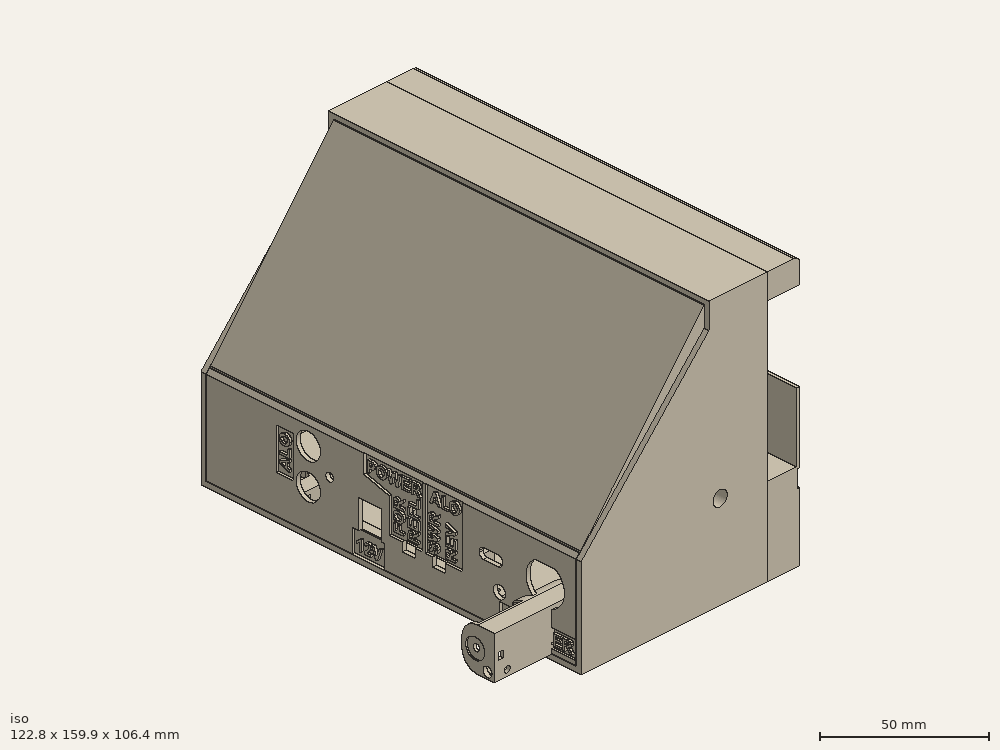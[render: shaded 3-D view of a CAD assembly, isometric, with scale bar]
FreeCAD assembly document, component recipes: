
FREECAD ASSEMBLY — COMPONENT RECIPES ("console")

This assembly document has 6 components, labeled P0..P5 below (a component is one placed body or linked part). 5 of them carry a construction recipe — the FreeCAD feature program that regenerates the part from scratch, quoted from this document or its linked companion documents; the rest are supplied as boundary geometry only. No exploded tour is included for this assembly.
NOTE — document 2 of 2 of this assembly tour. The two overview renders and the header above are repeated from document 1; the component sections below continue where the previous document stopped.
COMPONENT P5 — recipe-attached ("light pipe design", modeled in this document).
Construction recipe (the document's own serialized feature program — sketch geometry with constraints, then the solid features built on it; lengths are millimeters unless a unit is written):

FEATURE [PartDesign::SubShapeBinder] Binder016
  BindCopyOnChange = 0
  BindMode = 0
  ClaimChildren = false
  Context = -> Part004 [Body004.Binder016.]
  Fuse = false
  MakeFace = true
  OffsetFill = false
  OffsetIntersection = false
  OffsetJoinType = 0
  OffsetOpenResult = false
  PartialLoad = false
  Refine = true
  Relative = true
  Support = -> [Link003[PCB_Assembly.WP154A4SUREQBFZGC.,PCB_Assembly.WP154A4SUREQBFZGC001.,PCB_Assembly.WP154A4SUREQBFZGC002.,PCB_Assembly.WP154A4SUREQBFZGC003.,PCB_Assembly.WP154A4SUREQBFZGC004.,PCB_Assembly.WP154A4SUREQBFZGC005.]]
  _Version = 2
FEATURE [PartDesign::Plane] DatumPlane044  label="LED tips"
  AttachmentSupport = -> [Binder016]
  Length = 143.545
  MapMode = 5
  Placement = pos=(62.956,0,0) rot=(0.57735,0.57735,0.57735;2.0944rad)
  ResizeMode = 0
  Width = 66.0169
FEATURE [Sketcher::SketchObject] Sketch111  label="LED tip sketch"
  ArcFitTolerance = 1e-06
  AttachmentSupport = -> [DatumPlane044]
  ExternalGeometry = -> [Binder016]
  FullyConstrained = true
  MakeInternals = false
  MapMode = 5
  Placement = pos=(62.956,0,0) rot=(0.57735,0.57735,0.57735;2.0944rad)
  sketch-geometry (12):
    g0: Circle CenterX=15.113 CenterY=4.572 CenterZ=0 NormalX=0 NormalY=0 NormalZ=1 AngleXU=0 Radius=0.8
    g1: Circle CenterX=28.448 CenterY=4.572 CenterZ=0 NormalX=0 NormalY=0 NormalZ=1 AngleXU=0 Radius=0.8
    g2: Circle CenterX=50.038 CenterY=4.572 CenterZ=0 NormalX=0 NormalY=0 NormalZ=1 AngleXU=0 Radius=0.8
    g3: Circle CenterX=63.373 CenterY=4.572 CenterZ=0 NormalX=0 NormalY=0 NormalZ=1 AngleXU=0 Radius=0.8
    g4: Circle CenterX=84.963 CenterY=4.572 CenterZ=0 NormalX=0 NormalY=0 NormalZ=1 AngleXU=0 Radius=0.8
    g5: LineSegment StartX=84.963 StartY=4.572 StartZ=0 EndX=84.963 EndY=5.372 EndZ=0
    g6: LineSegment StartX=63.373 StartY=4.572 StartZ=0 EndX=63.373 EndY=5.372 EndZ=0
    g7: LineSegment StartX=50.038 StartY=4.572 StartZ=0 EndX=50.038 EndY=5.372 EndZ=0
    g8: LineSegment StartX=28.448 StartY=4.572 StartZ=0 EndX=28.448 EndY=5.372 EndZ=0
    g9: LineSegment StartX=15.113 StartY=4.572 StartZ=0 EndX=15.113 EndY=5.372 EndZ=0
    g10: Circle CenterX=98.298 CenterY=4.572 CenterZ=0 NormalX=0 NormalY=0 NormalZ=1 AngleXU=0 Radius=0.8
    g11: LineSegment StartX=98.298 StartY=4.572 StartZ=0 EndX=98.298 EndY=5.372 EndZ=0
  constraints (24):
    c: Coincident(g0,g-7)
    c: PointOnObject(g-7,g0)
    c: Coincident(g1,g-6)
    c: PointOnObject(g-6,g1)
    c: Coincident(g2,g-5)
    c: PointOnObject(g-5,g2)
    c: Coincident(g3,g-4)
    c: PointOnObject(g-4,g3)
    c: Coincident(g4,g-3)
    c: PointOnObject(g-3,g4)
    c: Coincident(g5,g4)
    c: Coincident(g5,g-3)
    c: Coincident(g6,g3)
    c: Coincident(g6,g-4)
    c: Coincident(g7,g2)
    c: Coincident(g7,g-5)
    c: Coincident(g8,g1)
    c: Coincident(g8,g-6)
    c: Coincident(g9,g0)
    c: Coincident(g9,g-7)
    c: Coincident(g10,g-8)
    c: PointOnObject(g-8,g10)
    c: Coincident(g11,g10)
    c: Coincident(g11,g-8)
FEATURE [PartDesign::Plane] DatumPlane045  label="inside sub break plane"
  AttachmentOffset = pos=(0,0,7.62) rot=(0,0,1;0rad)
  AttachmentSupport = -> [DatumPlane044]
  Length = 143.545
  MapMode = 2
  Placement = pos=(70.576,0,0) rot=(0.57735,0.57735,0.57735;2.0944rad)
  ResizeMode = 0
  Width = 66.0169
FEATURE [Sketcher::SketchObject] Sketch112
  ArcFitTolerance = 1e-06
  AttachmentSupport = -> [DatumPlane045]
  ExternalGeometry = -> [Sketch111]
  FullyConstrained = true
  MakeInternals = false
  MapMode = 5
  Placement = pos=(70.576,0,0) rot=(0.57735,0.57735,0.57735;2.0944rad)
  sketch-geometry (6):
    g0: LineSegment StartX=15.113 StartY=4.572 StartZ=0 EndX=15.113 EndY=5.372 EndZ=0
    g1: LineSegment StartX=28.448 StartY=4.572 StartZ=0 EndX=28.448 EndY=5.372 EndZ=0
    g2: LineSegment StartX=50.038 StartY=4.572 StartZ=0 EndX=50.038 EndY=5.372 EndZ=0
    g3: LineSegment StartX=63.373 StartY=4.572 StartZ=0 EndX=63.373 EndY=5.372 EndZ=0
    g4: LineSegment StartX=84.963 StartY=4.572 StartZ=0 EndX=84.963 EndY=5.372 EndZ=0
    g5: LineSegment StartX=98.298 StartY=4.572 StartZ=0 EndX=98.298 EndY=5.372 EndZ=0
  constraints (12):
    c: Coincident(g0,g-7)
    c: Coincident(g0,g-7)
    c: Coincident(g1,g-6)
    c: Coincident(g1,g-6)
    c: Coincident(g2,g-5)
    c: Coincident(g2,g-5)
    c: Coincident(g3,g-4)
    c: Coincident(g3,g-4)
    c: Coincident(g4,g-3)
    c: Coincident(g4,g-3)
    c: Coincident(g-8,g5)
    c: Coincident(g-8,g5)
FEATURE [PartDesign::Plane] DatumPlane046  label="LED initial pipe path"
  AttachmentSupport = -> [Sketch112,Sketch111]
  Length = 140.449
  MapMode = 13
  Placement = pos=(68.036,93.853,4.572) rot=(0,0,1;0rad)
  ResizeMode = 0
  Width = 151.907
FEATURE [Sketcher::SketchObject] Sketch003
  ArcFitTolerance = 1e-06
  AttachmentSupport = -> [DatumPlane046]
  ExternalGeometry = -> [Binder016,Sketch112]
  FullyConstrained = true
  MakeInternals = false
  MapMode = 5
  Placement = pos=(68.036,93.853,4.572) rot=(0,0,1;0rad)
  sketch-geometry (6):
    g0: LineSegment StartX=-5.08 StartY=4.445 StartZ=0 EndX=2.54 EndY=4.445 EndZ=0
    g1: LineSegment StartX=2.54 StartY=-8.89 StartZ=0 EndX=-5.08 EndY=-8.89 EndZ=0
    g2: LineSegment StartX=-5.08 StartY=-78.74 StartZ=0 EndX=2.54 EndY=-78.74 EndZ=0
    g3: LineSegment StartX=2.54 StartY=-65.405 StartZ=0 EndX=-5.08 EndY=-65.405 EndZ=0
    g4: LineSegment StartX=-5.08 StartY=-43.815 StartZ=0 EndX=2.54 EndY=-43.815 EndZ=0
    g5: LineSegment StartX=2.54 StartY=-30.48 StartZ=0 EndX=-5.08 EndY=-30.48 EndZ=0
  constraints (12):
    c: Coincident(g0,g-3)
    c: Coincident(g1,g-5)
    c: Coincident(g1,g-6)
    c: Coincident(g2,g-13)
    c: Coincident(g2,g-14)
    c: Coincident(g3,g-12)
    c: Coincident(g3,g-11)
    c: Coincident(g4,g-9)
    c: Coincident(g4,g-10)
    c: Coincident(g5,g-7)
    c: Coincident(g5,g-8)
    c: Coincident(g0,g-15)
FEATURE [PartDesign::SubShapeBinder] Binder002
  BindCopyOnChange = 0
  BindMode = 0
  ClaimChildren = false
  Context = -> Part004 [Body004.Binder002.]
  Fuse = false
  MakeFace = true
  OffsetFill = false
  OffsetIntersection = false
  OffsetJoinType = 0
  OffsetOpenResult = false
  PartialLoad = false
  Refine = true
  Relative = true
  Support = -> [Link003[PCB_Assembly.pcb_imported.]]
  _Version = 2
FEATURE [PartDesign::SubShapeBinder] Binder017
  BindCopyOnChange = 0
  BindMode = 0
  ClaimChildren = false
  Context = -> Part004 [Body004.Binder017.]
  Fuse = false
  MakeFace = true
  OffsetFill = false
  OffsetIntersection = false
  OffsetJoinType = 0
  OffsetOpenResult = false
  PartialLoad = false
  Refine = true
  Relative = true
  Support = -> [Link003[meter.,meter001.]]
  _Version = 2
FEATURE [PartDesign::SubShapeBinder] Binder018
  BindCopyOnChange = 0
  BindMode = 0
  ClaimChildren = false
  Context = -> Part004 [Body004.Binder018.]
  Fuse = false
  MakeFace = true
  OffsetFill = false
  OffsetIntersection = false
  OffsetJoinType = 0
  OffsetOpenResult = false
  PartialLoad = false
  Refine = true
  Relative = true
  Support = -> [Link003[_M_pot.]]
  _Version = 2
FEATURE [PartDesign::Plane] DatumPlane047  label="forward of front panel"
  AttachmentOffset = pos=(0,0,2.54) rot=(0,0,1;4.71239rad)
  AttachmentSupport = -> [Binder018]
  Length = 143.545
  MapMode = 11
  Placement = pos=(91.0899,-6.858,7.62) rot=(-0.57735,-0.57735,-0.57735;4.18879rad)
  ResizeMode = 0
  Width = 66.0169
FEATURE [Sketcher::SketchObject] Sketch113  label="FP LED positions"
  ArcFitTolerance = 1e-06
  AttachmentSupport = -> [DatumPlane047]
  ExternalGeometry = -> [Binder016,Binder002,Binder017]
  FullyConstrained = true
  MakeInternals = false
  MapMode = 5
  Placement = pos=(91.0899,-6.858,7.62) rot=(0.57735,0.57735,0.57735;2.0944rad)
  sketch-geometry (15):
    g0: Circle CenterX=74.008 CenterY=12.7 CenterZ=0 NormalX=0 NormalY=0 NormalZ=1 AngleXU=0 Radius=1
    g1: Circle CenterX=83.8403 CenterY=12.7 CenterZ=0 NormalX=0 NormalY=0 NormalZ=1 AngleXU=0 Radius=1
    g2: Circle CenterX=74.008 CenterY=0.18542 CenterZ=0 NormalX=0 NormalY=0 NormalZ=1 AngleXU=0 Radius=1
    g3: Circle CenterX=83.8403 CenterY=0.18542 CenterZ=0 NormalX=0 NormalY=0 NormalZ=1 AngleXU=0 Radius=1
    g4: Circle CenterX=74.008 CenterY=-12.3292 CenterZ=0 NormalX=0 NormalY=0 NormalZ=1 AngleXU=0 Radius=1
    g5: Circle CenterX=83.8403 CenterY=-12.3292 CenterZ=0 NormalX=0 NormalY=0 NormalZ=1 AngleXU=0 Radius=1
    g6: LineSegment [constr] StartX=74.008 StartY=12.7 StartZ=0 EndX=74.008 EndY=0.18542 EndZ=0
    g7: LineSegment [constr] StartX=74.008 StartY=0.18542 StartZ=0 EndX=74.008 EndY=-12.3292 EndZ=0
    g8: LineSegment StartX=83.8403 StartY=13.7 StartZ=0 EndX=83.8403 EndY=11.7 EndZ=0
    g9: LineSegment StartX=84.8403 StartY=12.7 StartZ=0 EndX=83.8403 EndY=12.7 EndZ=0
    g10: LineSegment StartX=74.008 StartY=12.7 StartZ=0 EndX=75.008 EndY=12.7 EndZ=0
    g11: LineSegment StartX=74.008 StartY=0.18542 StartZ=0 EndX=75.008 EndY=0.18542 EndZ=0
    g12: LineSegment StartX=83.8403 StartY=0.18542 StartZ=0 EndX=84.8403 EndY=0.18542 EndZ=0
    g13: LineSegment StartX=83.8403 StartY=-12.3292 StartZ=0 EndX=84.8403 EndY=-12.3292 EndZ=0
    g14: LineSegment StartX=74.008 StartY=-12.3292 StartZ=0 EndX=75.008 EndY=-12.3292 EndZ=0
  constraints (44):
    c: Equal(g0,g1)
    c: Equal(g0,g3)
    c: Equal(g0,g2)
    c: Equal(g0,g4)
    c: Equal(g0,g5)
    c: Diameter(g0) = 2
    c: Horizontal(g0,g1)
    c: Horizontal(g2,g3)
    c: Horizontal(g4,g5)
    c: Vertical(g1,g3)
    c: Vertical(g3,g5)
    c: DistanceX(g0,g1) = 9.83234
    c: Coincident(g6,g0)
    c: Coincident(g6,g2)
    c: Coincident(g7,g2)
    c: Coincident(g7,g4)
    c: Vertical(g6)
    c: Vertical(g7)
    c: Equal(g6,g7)
    c: DistanceY(g2,g0) = 12.5146
    c: DistanceX(g0,g-9) = 34.45
    c: DistanceY(g-9,g0) = 20.32
    c: PointOnObject(g8,g1)
    c: PointOnObject(g8,g1)
    c: PointOnObject(g9,g1)
    c: Horizontal(g9)
    c: Perpendicular(g1,g9)
    c: Perpendicular(g1,g8)
    c: Perpendicular(g9,g8) = 1.5708
    c: Coincident(g10,g0)
    c: PointOnObject(g10,g0)
    c: Horizontal(g10)
    c: Coincident(g11,g2)
    c: PointOnObject(g11,g2)
    c: Horizontal(g11)
    c: Coincident(g12,g3)
    c: PointOnObject(g12,g3)
    c: Coincident(g13,g5)
    c: PointOnObject(g13,g5)
    c: Horizontal(g13)
    c: Coincident(g14,g4)
    c: PointOnObject(g14,g4)
    c: Horizontal(g14)
    c: Horizontal(g12)
FEATURE [PartDesign::Plane] DatumPlane048  label="inside FP break plane"
  AttachmentOffset = pos=(0,0,-7.62) rot=(0,0,1;0rad)
  AttachmentSupport = -> [DatumPlane047]
  Length = 143.545
  MapMode = 2
  Placement = pos=(83.4699,-6.858,7.62) rot=(0.57735,0.57735,0.57735;2.0944rad)
  ResizeMode = 0
  Width = 66.0169
FEATURE [Sketcher::SketchObject] Sketch114
  ArcFitTolerance = 1e-06
  AttachmentSupport = -> [DatumPlane048]
  ExternalGeometry = -> [Sketch113]
  FullyConstrained = true
  MakeInternals = false
  MapMode = 5
  Placement = pos=(83.4699,-6.858,7.62) rot=(0.57735,0.57735,0.57735;2.0944rad)
  sketch-geometry (6):
    g0: LineSegment StartX=84.8403 StartY=-12.3292 StartZ=0 EndX=83.8403 EndY=-12.3292 EndZ=0
    g1: LineSegment StartX=75.008 StartY=-12.3292 StartZ=0 EndX=74.008 EndY=-12.3292 EndZ=0
    g2: LineSegment StartX=84.8403 StartY=0.18542 StartZ=0 EndX=83.8403 EndY=0.18542 EndZ=0
    g3: LineSegment StartX=75.008 StartY=0.18542 StartZ=0 EndX=74.008 EndY=0.18542 EndZ=0
    g4: LineSegment StartX=75.008 StartY=12.7 StartZ=0 EndX=74.008 EndY=12.7 EndZ=0
    g5: LineSegment StartX=83.8403 StartY=12.7 StartZ=0 EndX=84.8403 EndY=12.7 EndZ=0
  constraints (12):
    c: Coincident(g0,g-9)
    c: Coincident(g0,g-9)
    c: Coincident(g1,g-8)
    c: Coincident(g1,g-8)
    c: Coincident(g2,g-7)
    c: Coincident(g2,g-7)
    c: Coincident(g3,g-6)
    c: Coincident(g3,g-6)
    c: Coincident(g4,g-5)
    c: Coincident(g4,g-5)
    c: Symmetric(g-4,g-4,g5)
    c: Coincident(g5,g-3)
FEATURE [PartDesign::Plane] DatumPlane049  label="pipe 1 plane"
  AttachmentSupport = -> [Sketch003,Sketch113]
  Length = 140.9
  MapMode = 13
  Placement = pos=(74.874,91.1928,9.82133) rot=(1,0,0;2.5053rad)
  ResizeMode = 0
  Width = 157.127
FEATURE [Sketcher::SketchObject] Sketch115
  ArcFitTolerance = 1e-06
  AttachmentSupport = -> [DatumPlane049]
  ExternalGeometry = -> [Sketch113,Sketch003,Sketch114]
  FullyConstrained = true
  MakeInternals = false
  MapMode = 5
  Placement = pos=(74.874,91.1928,9.82133) rot=(1,0,0;2.5053rad)
  expr: Constraints[15] = <<Spreadsheet001>>.Base_PipeTurnRadius
  sketch-geometry (8):
    g0: LineSegment [constr] StartX=8.59592 StartY=17.668 StartZ=0 EndX=16.2159 EndY=17.668 EndZ=0
    g1: LineSegment StartX=-11.918 StartY=-8.83401 StartZ=0 EndX=-9.06464 EndY=-8.83401 EndZ=0
    g2: LineSegment StartX=-2.21257 StartY=-4.54771 StartZ=0 EndX=6.51053 EndY=13.3817 EndZ=0
    g3: LineSegment StartX=13.3626 StartY=17.668 StartZ=0 EndX=16.2159 EndY=17.668 EndZ=0
    g4: ArcOfCircle CenterX=13.3626 CenterY=10.048 CenterZ=0 NormalX=0 NormalY=0 NormalZ=1 AngleXU=0 Radius=7.62 StartAngle=1.5708 EndAngle=2.68878
    g5: GeomPoint [constr] X=8.59592 Y=17.668 Z=0
    g6: ArcOfCircle CenterX=-9.06464 CenterY=-1.21401 CenterZ=0 NormalX=0 NormalY=0 NormalZ=1 AngleXU=0 Radius=7.62 StartAngle=4.71239 EndAngle=5.83038
    g7: GeomPoint [constr] X=-4.29796 Y=-8.83401 Z=0
  constraints (16):
    c: Coincident(g0,g-7)
    c: Coincident(g0,g-5) = -1.5708
    c: Coincident(g1,g-6)
    c: Coincident(g7,g-6)
    c: Coincident(g5,g0)
    c: Coincident(g3,g0)
    c: PointOnObject(g5,g3)
    c: PointOnObject(g5,g2)
    c: Tangent(g3,g4) = 1.5708
    c: Tangent(g2,g4) = 1.5708
    c: PointOnObject(g7,g2)
    c: PointOnObject(g7,g1)
    c: Tangent(g2,g6) = -1.5708
    c: Tangent(g1,g6) = -1.5708
    c: Equal(g6,g4)
    c: Radius(g4) = 7.62
FEATURE [Sketcher::SketchObject] Sketch011
  ArcFitTolerance = 1e-06
  AttachmentSupport = -> [DatumPlane047]
  ExternalGeometry = -> [Sketch113]
  FullyConstrained = true
  MakeInternals = false
  MapMode = 5
  Placement = pos=(91.0899,-6.858,7.62) rot=(0.57735,0.57735,0.57735;2.0944rad)
  expr: Constraints[1] = <<Spreadsheet001>>.Base_PipID
  sketch-geometry (1):
    g0: Circle CenterX=83.8403 CenterY=12.7 CenterZ=0 NormalX=0 NormalY=0 NormalZ=1 AngleXU=0 Radius=1.5
  constraints (2):
    c: Coincident(g0,g-3)
    c: Diameter(g0) = 3
FEATURE [Sketcher::SketchObject] Sketch010
  ArcFitTolerance = 1e-06
  AttachmentSupport = -> [DatumPlane047]
  FullyConstrained = false
  MakeInternals = false
  MapMode = 5
  Placement = pos=(91.0899,-6.858,7.62) rot=(0.57735,0.57735,0.57735;2.0944rad)
  sketch-geometry (4):
    g0: LineSegment StartX=86.577 StartY=15.1029 StartZ=0 EndX=70.7785 EndY=15.1029 EndZ=0
    g1: LineSegment StartX=70.7785 StartY=15.1029 StartZ=0 EndX=70.7785 EndY=-17.1878 EndZ=0
    g2: LineSegment StartX=70.7785 StartY=-17.1878 StartZ=0 EndX=86.577 EndY=-17.1878 EndZ=0
    g3: LineSegment StartX=86.577 StartY=-17.1878 StartZ=0 EndX=86.577 EndY=15.1029 EndZ=0
  constraints (8):
    c: Coincident(g0,g1)
    c: Coincident(g1,g2)
    c: Coincident(g2,g3)
    c: Coincident(g3,g0)
    c: Horizontal(g0)
    c: Horizontal(g2)
    c: Vertical(g1)
    c: Vertical(g3)
FEATURE [Sketcher::SketchObject] Sketch006
  ArcFitTolerance = 1e-06
  AttachmentSupport = -> [DatumPlane047]
  ExternalGeometry = -> [Sketch113]
  FullyConstrained = true
  MakeInternals = false
  MapMode = 5
  Placement = pos=(91.0899,-6.858,7.62) rot=(0.57735,0.57735,0.57735;2.0944rad)
  expr: Constraints[1] = <<Spreadsheet001>>.Base_PipeOD
  sketch-geometry (1):
    g0: Circle CenterX=83.8403 CenterY=12.7 CenterZ=0 NormalX=0 NormalY=0 NormalZ=1 AngleXU=0 Radius=4.24942
  constraints (2):
    c: Coincident(g0,g-3)
    c: Diameter(g0) = 8.49884
FEATURE [PartDesign::Pad] Pad037
  Direction = (1,0,0)
  Length = 0.127
  Length2 = 10
  Placement = pos=(91.0899,-6.858,7.62) rot=(-0.57735,-0.57735,-0.57735;4.18879rad)
  Profile = -> Sketch010
  ReferenceAxis = -> Sketch010 [N_Axis]
  Refine = true
  Reversed = true
  Suppressed = false
  Type = 0
FEATURE [PartDesign::AdditivePipe] AdditivePipe
  AuxilleryCurvelinear = true
  AuxillerySpineTangent = false
  BaseFeature = -> Pad037
  Binormal = (0,0,0)
  Mode = 0
  Placement = pos=(91.0899,-6.858,7.62) rot=(-0.57735,-0.57735,-0.57735;4.18879rad)
  Profile = -> Sketch006
  Refine = true
  Spine = -> Sketch115
  SpineTangent = false
  Suppressed = false
  Transformation = 0
  Transition = 0
FEATURE [PartDesign::Plane] DatumPlane050  label="pipe 2 plane"
  AttachmentSupport = -> [Sketch003,Sketch113]
  Length = 140.559
  MapMode = 13
  Placement = pos=(74.874,79.0253,9.82133) rot=(0,0.35412,0.9352;3.14159rad)
  ResizeMode = 0
  Width = 153.165
FEATURE [Sketcher::SketchObject] Sketch008
  ArcFitTolerance = 1e-06
  AttachmentSupport = -> [DatumPlane050]
  ExternalGeometry = -> [Sketch003,Sketch114,Sketch113]
  FullyConstrained = true
  MakeInternals = false
  MapMode = 5
  Placement = pos=(74.874,79.0253,9.82133) rot=(0,0.35412,0.9352;3.14159rad)
  expr: Constraints[13] = <<Spreadsheet001>>.Base_PipeTurnRadius
  sketch-geometry (7):
    g0: LineSegment StartX=-16.2159 StartY=15.8507 StartZ=0 EndX=-13.1319 EndY=15.8507 EndZ=0
    g1: LineSegment StartX=-6.43352 StartY=11.8633 StartZ=0 EndX=2.13556 EndY=-3.93795 EndZ=0
    g2: LineSegment StartX=8.83398 StartY=-7.92537 StartZ=0 EndX=11.918 EndY=-7.92537 EndZ=0
    g3: ArcOfCircle CenterX=-13.1319 CenterY=8.23074 CenterZ=0 NormalX=0 NormalY=0 NormalZ=1 AngleXU=0 Radius=7.62 StartAngle=0.496915 EndAngle=1.5708
    g4: GeomPoint [constr] X=-8.59592 Y=15.8507 Z=0
    g5: ArcOfCircle CenterX=8.83398 CenterY=-0.305368 CenterZ=0 NormalX=0 NormalY=0 NormalZ=1 AngleXU=0 Radius=7.62 StartAngle=3.63851 EndAngle=4.71239
    g6: GeomPoint [constr] X=4.29796 Y=-7.92537 Z=0
  constraints (14):
    c: Coincident(g0,g-5)
    c: Coincident(g4,g-4)
    c: Coincident(g6,g-3)
    c: Coincident(g2,g-3)
    c: PointOnObject(g4,g0)
    c: PointOnObject(g4,g1)
    c: Tangent(g0,g3) = 1.5708
    c: Tangent(g1,g3) = 1.5708
    c: PointOnObject(g6,g1)
    c: PointOnObject(g6,g2)
    c: Tangent(g1,g5) = -1.5708
    c: Tangent(g2,g5) = -1.5708
    c: Equal(g5,g3)
    c: Radius(g3) = 7.62
FEATURE [Sketcher::SketchObject] Sketch116
  ArcFitTolerance = 1e-06
  AttachmentSupport = -> [DatumPlane047]
  ExternalGeometry = -> [Sketch113,Sketch006]
  FullyConstrained = true
  MakeInternals = false
  MapMode = 5
  Placement = pos=(91.0899,-6.858,7.62) rot=(0.57735,0.57735,0.57735;2.0944rad)
  sketch-geometry (1):
    g0: Circle CenterX=74.008 CenterY=12.7 CenterZ=0 NormalX=0 NormalY=0 NormalZ=1 AngleXU=0 Radius=4.24942
  constraints (2):
    c: Coincident(g0,g-3)
    c: Equal(g0,g-4)
FEATURE [PartDesign::AdditivePipe] AdditivePipe001  label="AdditivePipe2"
  AuxilleryCurvelinear = true
  AuxillerySpineTangent = false
  BaseFeature = -> AdditivePipe
  Binormal = (0,0,0)
  Mode = 0
  Placement = pos=(91.0899,-6.858,7.62) rot=(-0.57735,-0.57735,-0.57735;4.18879rad)
  Profile = -> Sketch116
  Refine = true
  Spine = -> Sketch008
  SpineTangent = false
  Suppressed = false
  Transformation = 0
  Transition = 0
FEATURE [Sketcher::SketchObject] Sketch120
  ArcFitTolerance = 1e-06
  AttachmentSupport = -> [DatumPlane047]
  ExternalGeometry = -> [Sketch113,AdditivePipe001]
  FullyConstrained = true
  MakeInternals = false
  MapMode = 5
  Placement = pos=(91.0899,-6.858,7.62) rot=(0.57735,0.57735,0.57735;2.0944rad)
  expr: Constraints[1] = <<Spreadsheet001>>.Base_PipID
  sketch-geometry (1):
    g0: Circle CenterX=74.008 CenterY=12.7 CenterZ=0 NormalX=0 NormalY=0 NormalZ=1 AngleXU=0 Radius=1.5
  constraints (2):
    c: Coincident(g0,g-5)
    c: Diameter(g0) = 3
FEATURE [PartDesign::Plane] DatumPlane054  label="pipe 3 plane"
  AttachmentSupport = -> [Sketch003,Sketch113]
  Length = 141.211
  MapMode = 13
  Placement = pos=(74.874,67.9094,5.64981) rot=(0,0.993206,0.116368;3.14159rad)
  ResizeMode = 0
  Width = 160.781
FEATURE [PartDesign::Plane] DatumPlane055  label="pipe 4 plane"
  AttachmentSupport = -> [Sketch003,Sketch113]
  Length = 141.115
  MapMode = 13
  Placement = pos=(74.874,55.742,5.64981) rot=(1,0,0;0.186755rad)
  ResizeMode = 0
  Width = 159.645
FEATURE [PartDesign::Plane] DatumPlane056  label="pipe 5 plane"
  AttachmentSupport = -> [Sketch003,Sketch113]
  Length = 141.12
  MapMode = 13
  Placement = pos=(74.874,44.6261,1.47828) rot=(1,0,0;2.95264rad)
  ResizeMode = 0
  Width = 159.706
FEATURE [PartDesign::Plane] DatumPlane057  label="pipe 6 plane"
  AttachmentSupport = -> [Sketch003,Sketch113]
  Length = 141.09
  MapMode = 13
  Placement = pos=(74.874,32.4587,1.47828) rot=(0,0.088136,0.996108;3.14159rad)
  ResizeMode = 0
  Width = 159.352
FEATURE [Sketcher::SketchObject] Sketch121  label="pipe 3 path"
  ArcFitTolerance = 1e-06
  AttachmentSupport = -> [DatumPlane054]
  ExternalGeometry = -> [Sketch003,Sketch113,Sketch114]
  FullyConstrained = true
  MakeInternals = false
  MapMode = 5
  Placement = pos=(74.874,67.9094,5.64981) rot=(0,0.993206,0.116368;3.14159rad)
  expr: Constraints[13] = <<Spreadsheet001>>.Base_PipeTurnRadius
  sketch-geometry (7):
    g0: LineSegment StartX=2.03459 StartY=-2.20726 StartZ=0 EndX=-6.33255 EndY=6.86998 EndZ=0
    g1: LineSegment StartX=-16.2159 StartY=9.32544 StartZ=0 EndX=-11.9354 EndY=9.32544 EndZ=0
    g2: LineSegment StartX=11.918 StartY=-4.66272 StartZ=0 EndX=7.63744 EndY=-4.66272 EndZ=0
    g3: ArcOfCircle CenterX=-11.9354 CenterY=1.70544 CenterZ=0 NormalX=0 NormalY=0 NormalZ=1 AngleXU=0 Radius=7.62 StartAngle=0.744714 EndAngle=1.5708
    g4: GeomPoint [constr] X=-8.59592 Y=9.32544 Z=0
    g5: ArcOfCircle CenterX=7.63744 CenterY=2.95728 CenterZ=0 NormalX=0 NormalY=0 NormalZ=1 AngleXU=0 Radius=7.62 StartAngle=3.88631 EndAngle=4.71239
    g6: GeomPoint [constr] X=4.29796 Y=-4.66272 Z=0
  constraints (14):
    c: Coincident(g1,g-4)
    c: Coincident(g4,g-5)
    c: Coincident(g6,g-3)
    c: Coincident(g2,g-3)
    c: PointOnObject(g4,g1)
    c: PointOnObject(g4,g0)
    c: Tangent(g1,g3) = 1.5708
    c: Tangent(g0,g3) = -1.5708
    c: PointOnObject(g6,g2)
    c: PointOnObject(g6,g0)
    c: Tangent(g2,g5) = 1.5708
    c: Tangent(g0,g5) = 1.5708
    c: Equal(g3,g5)
    c: Radius(g5) = 7.62
FEATURE [Sketcher::SketchObject] Sketch122  label="pipe 4 path"
  ArcFitTolerance = 1e-06
  AttachmentSupport = -> [DatumPlane055]
  ExternalGeometry = -> [Sketch003,Sketch113,Sketch114]
  FullyConstrained = true
  MakeInternals = false
  MapMode = 5
  Placement = pos=(74.874,55.742,5.64981) rot=(1,0,0;0.186755rad)
  expr: Constraints[15] = <<Spreadsheet001>>.Base_PipeTurnRadius
  sketch-geometry (9):
    g0: LineSegment StartX=-11.918 StartY=-5.80493 StartZ=0 EndX=-8.13741 EndY=-5.80493 EndZ=0
    g1: LineSegment StartX=16.2159 StartY=11.6099 StartZ=0 EndX=12.4354 EndY=11.6099 EndZ=0
    g2: LineSegment StartX=6.31126 StartY=8.52414 StartZ=0 EndX=-2.0133 EndY=-2.71921 EndZ=0
    g3: GeomPoint [constr] X=8.59592 Y=11.6099 Z=0
    g4: GeomPoint [constr] X=-4.29796 Y=-5.80493 Z=0
    g5: ArcOfCircle CenterX=12.4354 CenterY=3.98986 CenterZ=0 NormalX=0 NormalY=0 NormalZ=1 AngleXU=0 Radius=7.62 StartAngle=1.5708 EndAngle=2.50427
    g6: GeomPoint [constr] X=8.59592 Y=11.6099 Z=0
    g7: ArcOfCircle CenterX=-8.13741 CenterY=1.81507 CenterZ=0 NormalX=0 NormalY=0 NormalZ=1 AngleXU=0 Radius=7.62 StartAngle=4.71239 EndAngle=5.64586
    g8: GeomPoint [constr] X=-4.29796 Y=-5.80493 Z=0
  constraints (16):
    c: Coincident(g6,g3)
    c: Coincident(g6,g-5)
    c: Coincident(g8,g4)
    c: Coincident(g8,g-3)
    c: Coincident(g-3,g0)
    c: Coincident(g-4,g1)
    c: PointOnObject(g6,g1)
    c: PointOnObject(g6,g2)
    c: Tangent(g1,g5) = -1.5708
    c: Tangent(g2,g5) = -1.5708
    c: PointOnObject(g8,g0)
    c: PointOnObject(g8,g2)
    c: Tangent(g0,g7) = -1.5708
    c: Tangent(g2,g7) = 1.5708
    c: Equal(g7,g5)
    c: Radius(g5) = 7.62
FEATURE [Sketcher::SketchObject] Sketch123  label="pipe 5 path"
  ArcFitTolerance = 1e-06
  AttachmentSupport = -> [DatumPlane056]
  ExternalGeometry = -> [Sketch003,Sketch114,Sketch113]
  FullyConstrained = true
  MakeInternals = false
  MapMode = 5
  Placement = pos=(74.874,44.6261,1.47828) rot=(1,0,0;2.95264rad)
  expr: Constraints[13] = <<Spreadsheet001>>.Base_PipeTurnRadius
  sketch-geometry (7):
    g0: LineSegment StartX=-11.918 StartY=16.4713 StartZ=0 EndX=-10.1848 EndY=16.4713 EndZ=0
    g1: LineSegment StartX=-2.81164 StartY=10.7752 StartZ=0 EndX=7.1096 EndY=-27.2464 EndZ=0
    g2: LineSegment StartX=16.2159 StartY=-32.9425 StartZ=0 EndX=14.4827 EndY=-32.9425 EndZ=0
    g3: ArcOfCircle CenterX=-10.1848 CenterY=8.85125 CenterZ=0 NormalX=0 NormalY=0 NormalZ=1 AngleXU=0 Radius=7.62 StartAngle=0.255246 EndAngle=1.5708
    g4: GeomPoint [constr] X=-4.29796 Y=16.4713 Z=0
    g5: ArcOfCircle CenterX=14.4827 CenterY=-25.3225 CenterZ=0 NormalX=0 NormalY=0 NormalZ=1 AngleXU=0 Radius=7.62 StartAngle=3.39684 EndAngle=4.71239
    g6: GeomPoint [constr] X=8.59592 Y=-32.9425 Z=0
  constraints (14):
    c: Coincident(g0,g-3)
    c: Coincident(g4,g-3)
    c: Coincident(g2,g-5)
    c: Coincident(g6,g-4)
    c: PointOnObject(g4,g0)
    c: PointOnObject(g4,g1)
    c: Tangent(g0,g3) = 1.5708
    c: Tangent(g1,g3) = 1.5708
    c: PointOnObject(g6,g2)
    c: PointOnObject(g6,g1)
    c: Tangent(g2,g5) = 1.5708
    c: Tangent(g1,g5) = -1.5708
    c: Equal(g3,g5)
    c: Radius(g3) = 7.62
FEATURE [PartDesign::Plane] DatumPlane059  label="sub panel front001"
  AttachmentSupport = -> [Binder017]
  Length = 143.545
  MapMode = 5
  Placement = pos=(76.55,0,0) rot=(0.57735,-0.57735,-0.57735;2.0944rad)
  ResizeMode = 0
  Width = 66.0169
FEATURE [PartDesign::Body] Body004
  AllowCompound = false
  Group = -> [Binder018,Binder016,Binder002,Binder017,Sketch010,Pad037,DatumPlane047,DatumPlane059,Sketch113,DatumPlane044,Sketch111,DatumPlane048,DatumPlane045,Sketch112,DatumPlane046,Sketch003,Sketch114,DatumPlane049,Sketch115,Sketch006,AdditivePipe,DatumPlane050,Sketch008,Sketch116,Sketch011,AdditivePipe001,Sketch120,DatumPlane054,DatumPlane055,DatumPlane056,DatumPlane057,Sketch121,Sketch122,Sketch123,+27 more]
  Origin = -> Origin010
  Tip = -> Pad045
PROVENANCE & LICENSES
A FreeCAD (.FCStd) document from a public repository crawl; recipes are the document's own serialized feature recipes (and, for linked parts, companion documents' recipes).
License: mit.
